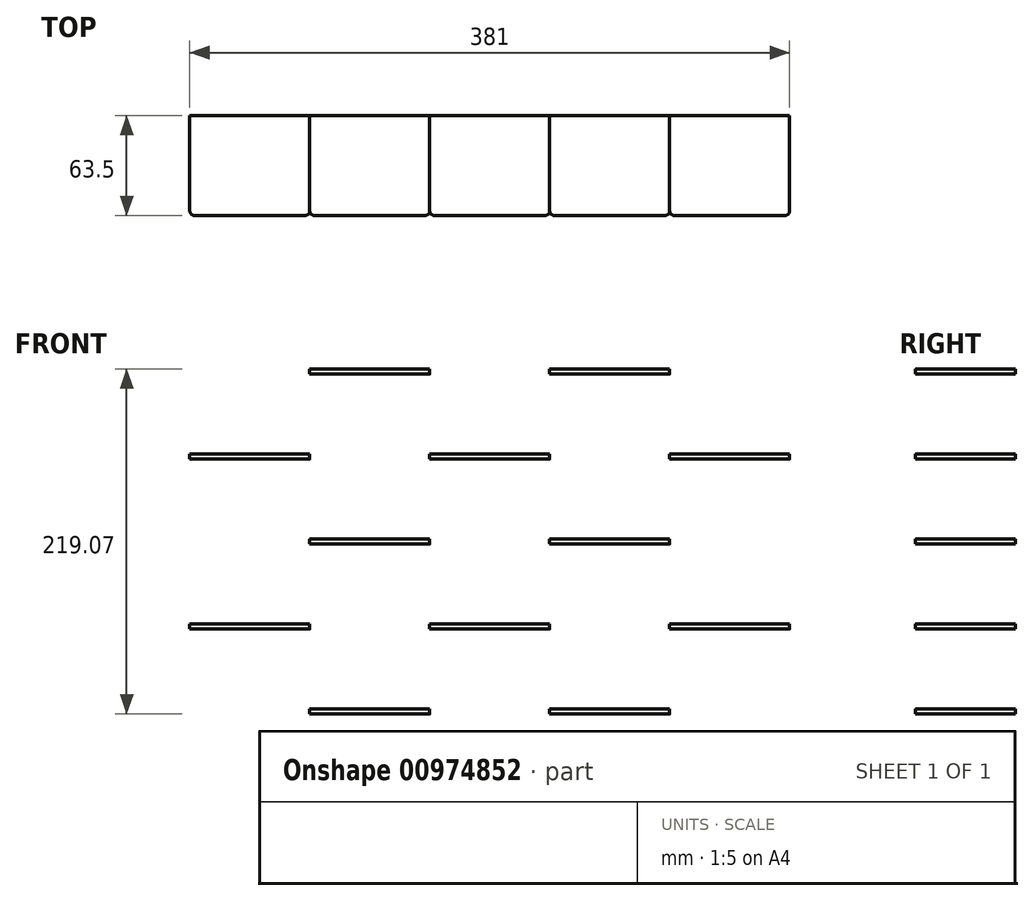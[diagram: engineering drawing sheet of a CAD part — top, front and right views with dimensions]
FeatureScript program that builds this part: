
annotation { "Feature Type Name" : "Feature", "Feature Type Description" : "" }
export const myFeature = defineFeature(function(context is Context, id is Id, definition is map)
    precondition{}
    {
        {
            var Q0;
            Q0=qCreatedBy(makeId("Front.planeOp"),FACE);
            var sketch = newSketch(context, id + "F0", { "sketchPlane" : qUnion([Q0])});
            skLineSegment(sketch, "E0.bottom", {"start": v(-97.67, 0) * mm, "end": v(-21.47, 0) * mm});
            skLineSegment(sketch, "E0.top", {"start": v(-97.67, -3.18) * mm, "end": v(-21.47, -3.18) * mm});
            skLineSegment(sketch, "E0.left", {"start": v(-97.67, 0) * mm, "end": v(-97.67, -3.18) * mm});
            skLineSegment(sketch, "E0.right", {"start": v(-21.47, 0) * mm, "end": v(-21.47, -3.18) * mm});
            skSolve(sketch);
        }
        {
            var Q0;
            Q0 = qSketchRegion(id + "F0", true);
            extrude(context, id + "F1", {"entities" : qUnion([Q0]), "depth" : 63.5 * mm, "offsetDistance" : 25.4 * mm});
        }
        {
            var Q0;
            Q0=makeQuery(id+"F1.opExtrude","CAP_EDGE",EDGE,{"disambiguationData":[OSD([sQuery(id+"F0.wireOp",EDGE,"E0.right")])],"isStart":false});
            fillet(context, id + "F2", {"entities" : qUnion([Q0]), "radius" : 3.17 * mm, "tangentPropagation" : true, "allowEdgeOverflow" : false});
        }
        {
            var Q0;
            Q0=makeQuery(id+"F1.opExtrude","CAP_EDGE",EDGE,{"disambiguationData":[OSD([sQuery(id+"F0.wireOp",EDGE,"E0.left")])],"isStart":false});
            fillet(context, id + "F3", {"entities" : qUnion([Q0]), "radius" : 3.17 * mm, "tangentPropagation" : true, "allowEdgeOverflow" : false});
        }
        {
            var Q0;
            Q0=makeQuery(id+"F1.opExtrude","SWEPT_BODY",BODY,{"disambiguationData":[OSD([sQuery(id+"F0.wireOp",EDGE,"E0.bottom"),sQuery(id+"F0.wireOp",EDGE,"E0.top"),sQuery(id+"F0.wireOp",EDGE,"E0.left"),sQuery(id+"F0.wireOp",EDGE,"E0.right")])]});
            transform(context, id + "F4", {"entities" : qUnion([Q0]), "transformType" : TransformType.TRANSLATION_3D, "dx" : 76.2 * mm, "dy" : 0 * mm, "dz" : 0 * mm, "makeCopy" : true});
        }
        {
            var Q0;
            Q0=makeQuery(id+"F4.opPattern","COPY",BODY,{"derivedFrom":makeQuery(id+"F1.opExtrude","SWEPT_BODY",BODY,{"disambiguationData":[OSD([sQuery(id+"F0.wireOp",EDGE,"E0.bottom"),sQuery(id+"F0.wireOp",EDGE,"E0.top"),sQuery(id+"F0.wireOp",EDGE,"E0.left"),sQuery(id+"F0.wireOp",EDGE,"E0.right")])]}),"instanceName":"1"});
            transform(context, id + "F5", {"entities" : qUnion([Q0]), "transformType" : TransformType.TRANSLATION_3D, "dx" : 76.2 * mm, "dy" : 0 * mm, "dz" : 0 * mm, "makeCopy" : true});
        }
        {
            var Q0;
            Q0=makeQuery(id+"F5.opPattern","COPY",BODY,{"derivedFrom":makeQuery(id+"F4.opPattern","COPY",BODY,{"derivedFrom":makeQuery(id+"F1.opExtrude","SWEPT_BODY",BODY,{"disambiguationData":[OSD([sQuery(id+"F0.wireOp",EDGE,"E0.bottom"),sQuery(id+"F0.wireOp",EDGE,"E0.top"),sQuery(id+"F0.wireOp",EDGE,"E0.left"),sQuery(id+"F0.wireOp",EDGE,"E0.right")])]}),"instanceName":"1"}),"instanceName":"1"});
            transform(context, id + "F6", {"entities" : qUnion([Q0]), "transformType" : TransformType.TRANSLATION_3D, "dx" : 76.2 * mm, "dy" : 0 * mm, "dz" : 0 * mm, "makeCopy" : true});
        }
        {
            var Q0;
            Q0=makeQuery(id+"F6.opPattern","COPY",BODY,{"derivedFrom":makeQuery(id+"F5.opPattern","COPY",BODY,{"derivedFrom":makeQuery(id+"F4.opPattern","COPY",BODY,{"derivedFrom":makeQuery(id+"F1.opExtrude","SWEPT_BODY",BODY,{"disambiguationData":[OSD([sQuery(id+"F0.wireOp",EDGE,"E0.bottom"),sQuery(id+"F0.wireOp",EDGE,"E0.top"),sQuery(id+"F0.wireOp",EDGE,"E0.left"),sQuery(id+"F0.wireOp",EDGE,"E0.right")])]}),"instanceName":"1"}),"instanceName":"1"}),"instanceName":"1"});
            transform(context, id + "F7", {"entities" : qUnion([Q0]), "transformType" : TransformType.TRANSLATION_3D, "dx" : 76.2 * mm, "dy" : 0 * mm, "dz" : 0 * mm, "makeCopy" : true});
        }
        {
            var Q0;
            Q0=makeQuery(id+"F1.opExtrude","SWEPT_BODY",BODY,{"disambiguationData":[OSD([sQuery(id+"F0.wireOp",EDGE,"E0.bottom"),sQuery(id+"F0.wireOp",EDGE,"E0.top"),sQuery(id+"F0.wireOp",EDGE,"E0.left"),sQuery(id+"F0.wireOp",EDGE,"E0.right")])]});
            var Q1;
            Q1=makeQuery(id+"F4.opPattern","COPY",BODY,{"derivedFrom":makeQuery(id+"F1.opExtrude","SWEPT_BODY",BODY,{"disambiguationData":[OSD([sQuery(id+"F0.wireOp",EDGE,"E0.bottom"),sQuery(id+"F0.wireOp",EDGE,"E0.top"),sQuery(id+"F0.wireOp",EDGE,"E0.left"),sQuery(id+"F0.wireOp",EDGE,"E0.right")])]}),"instanceName":"1"});
            var Q2;
            Q2=makeQuery(id+"F5.opPattern","COPY",BODY,{"derivedFrom":makeQuery(id+"F4.opPattern","COPY",BODY,{"derivedFrom":makeQuery(id+"F1.opExtrude","SWEPT_BODY",BODY,{"disambiguationData":[OSD([sQuery(id+"F0.wireOp",EDGE,"E0.bottom"),sQuery(id+"F0.wireOp",EDGE,"E0.top"),sQuery(id+"F0.wireOp",EDGE,"E0.left"),sQuery(id+"F0.wireOp",EDGE,"E0.right")])]}),"instanceName":"1"}),"instanceName":"1"});
            var Q3;
            Q3=makeQuery(id+"F6.opPattern","COPY",BODY,{"derivedFrom":makeQuery(id+"F5.opPattern","COPY",BODY,{"derivedFrom":makeQuery(id+"F4.opPattern","COPY",BODY,{"derivedFrom":makeQuery(id+"F1.opExtrude","SWEPT_BODY",BODY,{"disambiguationData":[OSD([sQuery(id+"F0.wireOp",EDGE,"E0.bottom"),sQuery(id+"F0.wireOp",EDGE,"E0.top"),sQuery(id+"F0.wireOp",EDGE,"E0.left"),sQuery(id+"F0.wireOp",EDGE,"E0.right")])]}),"instanceName":"1"}),"instanceName":"1"}),"instanceName":"1"});
            var Q4;
            Q4=makeQuery(id+"F7.opPattern","COPY",BODY,{"derivedFrom":makeQuery(id+"F6.opPattern","COPY",BODY,{"derivedFrom":makeQuery(id+"F5.opPattern","COPY",BODY,{"derivedFrom":makeQuery(id+"F4.opPattern","COPY",BODY,{"derivedFrom":makeQuery(id+"F1.opExtrude","SWEPT_BODY",BODY,{"disambiguationData":[OSD([sQuery(id+"F0.wireOp",EDGE,"E0.bottom"),sQuery(id+"F0.wireOp",EDGE,"E0.top"),sQuery(id+"F0.wireOp",EDGE,"E0.left"),sQuery(id+"F0.wireOp",EDGE,"E0.right")])]}),"instanceName":"1"}),"instanceName":"1"}),"instanceName":"1"}),"instanceName":"1"});
            transform(context, id + "F8", {"entities" : qUnion([Q0, Q1, Q2, Q3, Q4]), "transformType" : TransformType.TRANSLATION_3D, "dx" : 0 * mm, "dy" : 0 * mm, "dz" : 104.77 * mm, "makeCopy" : true});
        }
        {
            var Q0;
            Q0=makeQuery(id+"F8.opPattern","COPY",BODY,{"derivedFrom":makeQuery(id+"F1.opExtrude","SWEPT_BODY",BODY,{"disambiguationData":[OSD([sQuery(id+"F0.wireOp",EDGE,"E0.bottom"),sQuery(id+"F0.wireOp",EDGE,"E0.top"),sQuery(id+"F0.wireOp",EDGE,"E0.left"),sQuery(id+"F0.wireOp",EDGE,"E0.right")])]}),"instanceName":"1"});
            var Q1;
            Q1=makeQuery(id+"F8.opPattern","COPY",BODY,{"derivedFrom":makeQuery(id+"F4.opPattern","COPY",BODY,{"derivedFrom":makeQuery(id+"F1.opExtrude","SWEPT_BODY",BODY,{"disambiguationData":[OSD([sQuery(id+"F0.wireOp",EDGE,"E0.bottom"),sQuery(id+"F0.wireOp",EDGE,"E0.top"),sQuery(id+"F0.wireOp",EDGE,"E0.left"),sQuery(id+"F0.wireOp",EDGE,"E0.right")])]}),"instanceName":"1"}),"instanceName":"1"});
            var Q2;
            Q2=makeQuery(id+"F8.opPattern","COPY",BODY,{"derivedFrom":makeQuery(id+"F6.opPattern","COPY",BODY,{"derivedFrom":makeQuery(id+"F5.opPattern","COPY",BODY,{"derivedFrom":makeQuery(id+"F4.opPattern","COPY",BODY,{"derivedFrom":makeQuery(id+"F1.opExtrude","SWEPT_BODY",BODY,{"disambiguationData":[OSD([sQuery(id+"F0.wireOp",EDGE,"E0.bottom"),sQuery(id+"F0.wireOp",EDGE,"E0.top"),sQuery(id+"F0.wireOp",EDGE,"E0.left"),sQuery(id+"F0.wireOp",EDGE,"E0.right")])]}),"instanceName":"1"}),"instanceName":"1"}),"instanceName":"1"}),"instanceName":"1"});
            var Q3;
            Q3=makeQuery(id+"F8.opPattern","COPY",BODY,{"derivedFrom":makeQuery(id+"F7.opPattern","COPY",BODY,{"derivedFrom":makeQuery(id+"F6.opPattern","COPY",BODY,{"derivedFrom":makeQuery(id+"F5.opPattern","COPY",BODY,{"derivedFrom":makeQuery(id+"F4.opPattern","COPY",BODY,{"derivedFrom":makeQuery(id+"F1.opExtrude","SWEPT_BODY",BODY,{"disambiguationData":[OSD([sQuery(id+"F0.wireOp",EDGE,"E0.bottom"),sQuery(id+"F0.wireOp",EDGE,"E0.top"),sQuery(id+"F0.wireOp",EDGE,"E0.left"),sQuery(id+"F0.wireOp",EDGE,"E0.right")])]}),"instanceName":"1"}),"instanceName":"1"}),"instanceName":"1"}),"instanceName":"1"}),"instanceName":"1"});
            var Q4;
            Q4=makeQuery(id+"F8.opPattern","COPY",BODY,{"derivedFrom":makeQuery(id+"F5.opPattern","COPY",BODY,{"derivedFrom":makeQuery(id+"F4.opPattern","COPY",BODY,{"derivedFrom":makeQuery(id+"F1.opExtrude","SWEPT_BODY",BODY,{"disambiguationData":[OSD([sQuery(id+"F0.wireOp",EDGE,"E0.bottom"),sQuery(id+"F0.wireOp",EDGE,"E0.top"),sQuery(id+"F0.wireOp",EDGE,"E0.left"),sQuery(id+"F0.wireOp",EDGE,"E0.right")])]}),"instanceName":"1"}),"instanceName":"1"}),"instanceName":"1"});
            transform(context, id + "F9", {"entities" : qUnion([Q0, Q1, Q2, Q3, Q4]), "transformType" : TransformType.TRANSLATION_3D, "dx" : 0 * mm, "dy" : 0 * mm, "dz" : 127 * mm, "makeCopy" : true});
        }
        {
            var Q0;
            Q0=makeQuery(id+"F9.opPattern","COPY",BODY,{"derivedFrom":makeQuery(id+"F8.opPattern","COPY",BODY,{"derivedFrom":makeQuery(id+"F1.opExtrude","SWEPT_BODY",BODY,{"disambiguationData":[OSD([sQuery(id+"F0.wireOp",EDGE,"E0.bottom"),sQuery(id+"F0.wireOp",EDGE,"E0.top"),sQuery(id+"F0.wireOp",EDGE,"E0.left"),sQuery(id+"F0.wireOp",EDGE,"E0.right")])]}),"instanceName":"1"}),"instanceName":"1"});
            var Q1;
            Q1=makeQuery(id+"F9.opPattern","COPY",BODY,{"derivedFrom":makeQuery(id+"F8.opPattern","COPY",BODY,{"derivedFrom":makeQuery(id+"F4.opPattern","COPY",BODY,{"derivedFrom":makeQuery(id+"F1.opExtrude","SWEPT_BODY",BODY,{"disambiguationData":[OSD([sQuery(id+"F0.wireOp",EDGE,"E0.bottom"),sQuery(id+"F0.wireOp",EDGE,"E0.top"),sQuery(id+"F0.wireOp",EDGE,"E0.left"),sQuery(id+"F0.wireOp",EDGE,"E0.right")])]}),"instanceName":"1"}),"instanceName":"1"}),"instanceName":"1"});
            var Q2;
            Q2=makeQuery(id+"F9.opPattern","COPY",BODY,{"derivedFrom":makeQuery(id+"F8.opPattern","COPY",BODY,{"derivedFrom":makeQuery(id+"F5.opPattern","COPY",BODY,{"derivedFrom":makeQuery(id+"F4.opPattern","COPY",BODY,{"derivedFrom":makeQuery(id+"F1.opExtrude","SWEPT_BODY",BODY,{"disambiguationData":[OSD([sQuery(id+"F0.wireOp",EDGE,"E0.bottom"),sQuery(id+"F0.wireOp",EDGE,"E0.top"),sQuery(id+"F0.wireOp",EDGE,"E0.left"),sQuery(id+"F0.wireOp",EDGE,"E0.right")])]}),"instanceName":"1"}),"instanceName":"1"}),"instanceName":"1"}),"instanceName":"1"});
            var Q3;
            Q3=makeQuery(id+"F9.opPattern","COPY",BODY,{"derivedFrom":makeQuery(id+"F8.opPattern","COPY",BODY,{"derivedFrom":makeQuery(id+"F6.opPattern","COPY",BODY,{"derivedFrom":makeQuery(id+"F5.opPattern","COPY",BODY,{"derivedFrom":makeQuery(id+"F4.opPattern","COPY",BODY,{"derivedFrom":makeQuery(id+"F1.opExtrude","SWEPT_BODY",BODY,{"disambiguationData":[OSD([sQuery(id+"F0.wireOp",EDGE,"E0.bottom"),sQuery(id+"F0.wireOp",EDGE,"E0.top"),sQuery(id+"F0.wireOp",EDGE,"E0.left"),sQuery(id+"F0.wireOp",EDGE,"E0.right")])]}),"instanceName":"1"}),"instanceName":"1"}),"instanceName":"1"}),"instanceName":"1"}),"instanceName":"1"});
            var Q4;
            Q4=makeQuery(id+"F9.opPattern","COPY",BODY,{"derivedFrom":makeQuery(id+"F8.opPattern","COPY",BODY,{"derivedFrom":makeQuery(id+"F7.opPattern","COPY",BODY,{"derivedFrom":makeQuery(id+"F6.opPattern","COPY",BODY,{"derivedFrom":makeQuery(id+"F5.opPattern","COPY",BODY,{"derivedFrom":makeQuery(id+"F4.opPattern","COPY",BODY,{"derivedFrom":makeQuery(id+"F1.opExtrude","SWEPT_BODY",BODY,{"disambiguationData":[OSD([sQuery(id+"F0.wireOp",EDGE,"E0.bottom"),sQuery(id+"F0.wireOp",EDGE,"E0.top"),sQuery(id+"F0.wireOp",EDGE,"E0.left"),sQuery(id+"F0.wireOp",EDGE,"E0.right")])]}),"instanceName":"1"}),"instanceName":"1"}),"instanceName":"1"}),"instanceName":"1"}),"instanceName":"1"}),"instanceName":"1"});
            transform(context, id + "F10", {"entities" : qUnion([Q0, Q1, Q2, Q3, Q4]), "transformType" : TransformType.TRANSLATION_3D, "dx" : 0 * mm, "dy" : 0 * mm, "dz" : 104.77 * mm, "makeCopy" : true});
        }
        {
            var Q0;
            Q0=makeQuery(id+"F10.opPattern","COPY",BODY,{"derivedFrom":makeQuery(id+"F9.opPattern","COPY",BODY,{"derivedFrom":makeQuery(id+"F8.opPattern","COPY",BODY,{"derivedFrom":makeQuery(id+"F1.opExtrude","SWEPT_BODY",BODY,{"disambiguationData":[OSD([sQuery(id+"F0.wireOp",EDGE,"E0.bottom"),sQuery(id+"F0.wireOp",EDGE,"E0.top"),sQuery(id+"F0.wireOp",EDGE,"E0.left"),sQuery(id+"F0.wireOp",EDGE,"E0.right")])]}),"instanceName":"1"}),"instanceName":"1"}),"instanceName":"1"});
            var Q1;
            Q1=makeQuery(id+"F10.opPattern","COPY",BODY,{"derivedFrom":makeQuery(id+"F9.opPattern","COPY",BODY,{"derivedFrom":makeQuery(id+"F8.opPattern","COPY",BODY,{"derivedFrom":makeQuery(id+"F4.opPattern","COPY",BODY,{"derivedFrom":makeQuery(id+"F1.opExtrude","SWEPT_BODY",BODY,{"disambiguationData":[OSD([sQuery(id+"F0.wireOp",EDGE,"E0.bottom"),sQuery(id+"F0.wireOp",EDGE,"E0.top"),sQuery(id+"F0.wireOp",EDGE,"E0.left"),sQuery(id+"F0.wireOp",EDGE,"E0.right")])]}),"instanceName":"1"}),"instanceName":"1"}),"instanceName":"1"}),"instanceName":"1"});
            var Q2;
            Q2=makeQuery(id+"F10.opPattern","COPY",BODY,{"derivedFrom":makeQuery(id+"F9.opPattern","COPY",BODY,{"derivedFrom":makeQuery(id+"F8.opPattern","COPY",BODY,{"derivedFrom":makeQuery(id+"F5.opPattern","COPY",BODY,{"derivedFrom":makeQuery(id+"F4.opPattern","COPY",BODY,{"derivedFrom":makeQuery(id+"F1.opExtrude","SWEPT_BODY",BODY,{"disambiguationData":[OSD([sQuery(id+"F0.wireOp",EDGE,"E0.bottom"),sQuery(id+"F0.wireOp",EDGE,"E0.top"),sQuery(id+"F0.wireOp",EDGE,"E0.left"),sQuery(id+"F0.wireOp",EDGE,"E0.right")])]}),"instanceName":"1"}),"instanceName":"1"}),"instanceName":"1"}),"instanceName":"1"}),"instanceName":"1"});
            var Q3;
            Q3=makeQuery(id+"F10.opPattern","COPY",BODY,{"derivedFrom":makeQuery(id+"F9.opPattern","COPY",BODY,{"derivedFrom":makeQuery(id+"F8.opPattern","COPY",BODY,{"derivedFrom":makeQuery(id+"F6.opPattern","COPY",BODY,{"derivedFrom":makeQuery(id+"F5.opPattern","COPY",BODY,{"derivedFrom":makeQuery(id+"F4.opPattern","COPY",BODY,{"derivedFrom":makeQuery(id+"F1.opExtrude","SWEPT_BODY",BODY,{"disambiguationData":[OSD([sQuery(id+"F0.wireOp",EDGE,"E0.bottom"),sQuery(id+"F0.wireOp",EDGE,"E0.top"),sQuery(id+"F0.wireOp",EDGE,"E0.left"),sQuery(id+"F0.wireOp",EDGE,"E0.right")])]}),"instanceName":"1"}),"instanceName":"1"}),"instanceName":"1"}),"instanceName":"1"}),"instanceName":"1"}),"instanceName":"1"});
            var Q4;
            Q4=makeQuery(id+"F10.opPattern","COPY",BODY,{"derivedFrom":makeQuery(id+"F9.opPattern","COPY",BODY,{"derivedFrom":makeQuery(id+"F8.opPattern","COPY",BODY,{"derivedFrom":makeQuery(id+"F7.opPattern","COPY",BODY,{"derivedFrom":makeQuery(id+"F6.opPattern","COPY",BODY,{"derivedFrom":makeQuery(id+"F5.opPattern","COPY",BODY,{"derivedFrom":makeQuery(id+"F4.opPattern","COPY",BODY,{"derivedFrom":makeQuery(id+"F1.opExtrude","SWEPT_BODY",BODY,{"disambiguationData":[OSD([sQuery(id+"F0.wireOp",EDGE,"E0.bottom"),sQuery(id+"F0.wireOp",EDGE,"E0.top"),sQuery(id+"F0.wireOp",EDGE,"E0.left"),sQuery(id+"F0.wireOp",EDGE,"E0.right")])]}),"instanceName":"1"}),"instanceName":"1"}),"instanceName":"1"}),"instanceName":"1"}),"instanceName":"1"}),"instanceName":"1"}),"instanceName":"1"});
            transform(context, id + "F11", {"entities" : qUnion([Q0, Q1, Q2, Q3, Q4]), "transformType" : TransformType.TRANSLATION_3D, "dx" : 0 * mm, "dy" : 0 * mm, "dz" : 104.77 * mm, "makeCopy" : true});
        }
        {
            var Q0;
            Q0=makeQuery(id+"F10.opPattern","COPY",BODY,{"derivedFrom":makeQuery(id+"F9.opPattern","COPY",BODY,{"derivedFrom":makeQuery(id+"F8.opPattern","COPY",BODY,{"derivedFrom":makeQuery(id+"F7.opPattern","COPY",BODY,{"derivedFrom":makeQuery(id+"F6.opPattern","COPY",BODY,{"derivedFrom":makeQuery(id+"F5.opPattern","COPY",BODY,{"derivedFrom":makeQuery(id+"F4.opPattern","COPY",BODY,{"derivedFrom":makeQuery(id+"F1.opExtrude","SWEPT_BODY",BODY,{"disambiguationData":[OSD([sQuery(id+"F0.wireOp",EDGE,"E0.bottom"),sQuery(id+"F0.wireOp",EDGE,"E0.top"),sQuery(id+"F0.wireOp",EDGE,"E0.left"),sQuery(id+"F0.wireOp",EDGE,"E0.right")])]}),"instanceName":"1"}),"instanceName":"1"}),"instanceName":"1"}),"instanceName":"1"}),"instanceName":"1"}),"instanceName":"1"}),"instanceName":"1"});
            var Q1;
            Q1=makeQuery(id+"F10.opPattern","COPY",BODY,{"derivedFrom":makeQuery(id+"F9.opPattern","COPY",BODY,{"derivedFrom":makeQuery(id+"F8.opPattern","COPY",BODY,{"derivedFrom":makeQuery(id+"F6.opPattern","COPY",BODY,{"derivedFrom":makeQuery(id+"F5.opPattern","COPY",BODY,{"derivedFrom":makeQuery(id+"F4.opPattern","COPY",BODY,{"derivedFrom":makeQuery(id+"F1.opExtrude","SWEPT_BODY",BODY,{"disambiguationData":[OSD([sQuery(id+"F0.wireOp",EDGE,"E0.bottom"),sQuery(id+"F0.wireOp",EDGE,"E0.top"),sQuery(id+"F0.wireOp",EDGE,"E0.left"),sQuery(id+"F0.wireOp",EDGE,"E0.right")])]}),"instanceName":"1"}),"instanceName":"1"}),"instanceName":"1"}),"instanceName":"1"}),"instanceName":"1"}),"instanceName":"1"});
            var Q2;
            Q2=makeQuery(id+"F10.opPattern","COPY",BODY,{"derivedFrom":makeQuery(id+"F9.opPattern","COPY",BODY,{"derivedFrom":makeQuery(id+"F8.opPattern","COPY",BODY,{"derivedFrom":makeQuery(id+"F5.opPattern","COPY",BODY,{"derivedFrom":makeQuery(id+"F4.opPattern","COPY",BODY,{"derivedFrom":makeQuery(id+"F1.opExtrude","SWEPT_BODY",BODY,{"disambiguationData":[OSD([sQuery(id+"F0.wireOp",EDGE,"E0.bottom"),sQuery(id+"F0.wireOp",EDGE,"E0.top"),sQuery(id+"F0.wireOp",EDGE,"E0.left"),sQuery(id+"F0.wireOp",EDGE,"E0.right")])]}),"instanceName":"1"}),"instanceName":"1"}),"instanceName":"1"}),"instanceName":"1"}),"instanceName":"1"});
            var Q3;
            Q3=makeQuery(id+"F10.opPattern","COPY",BODY,{"derivedFrom":makeQuery(id+"F9.opPattern","COPY",BODY,{"derivedFrom":makeQuery(id+"F8.opPattern","COPY",BODY,{"derivedFrom":makeQuery(id+"F4.opPattern","COPY",BODY,{"derivedFrom":makeQuery(id+"F1.opExtrude","SWEPT_BODY",BODY,{"disambiguationData":[OSD([sQuery(id+"F0.wireOp",EDGE,"E0.bottom"),sQuery(id+"F0.wireOp",EDGE,"E0.top"),sQuery(id+"F0.wireOp",EDGE,"E0.left"),sQuery(id+"F0.wireOp",EDGE,"E0.right")])]}),"instanceName":"1"}),"instanceName":"1"}),"instanceName":"1"}),"instanceName":"1"});
            var Q4;
            Q4=makeQuery(id+"F10.opPattern","COPY",BODY,{"derivedFrom":makeQuery(id+"F9.opPattern","COPY",BODY,{"derivedFrom":makeQuery(id+"F8.opPattern","COPY",BODY,{"derivedFrom":makeQuery(id+"F1.opExtrude","SWEPT_BODY",BODY,{"disambiguationData":[OSD([sQuery(id+"F0.wireOp",EDGE,"E0.bottom"),sQuery(id+"F0.wireOp",EDGE,"E0.top"),sQuery(id+"F0.wireOp",EDGE,"E0.left"),sQuery(id+"F0.wireOp",EDGE,"E0.right")])]}),"instanceName":"1"}),"instanceName":"1"}),"instanceName":"1"});
            var Q5;
            Q5=makeQuery(id+"F9.opPattern","COPY",BODY,{"derivedFrom":makeQuery(id+"F8.opPattern","COPY",BODY,{"derivedFrom":makeQuery(id+"F1.opExtrude","SWEPT_BODY",BODY,{"disambiguationData":[OSD([sQuery(id+"F0.wireOp",EDGE,"E0.bottom"),sQuery(id+"F0.wireOp",EDGE,"E0.top"),sQuery(id+"F0.wireOp",EDGE,"E0.left"),sQuery(id+"F0.wireOp",EDGE,"E0.right")])]}),"instanceName":"1"}),"instanceName":"1"});
            var Q6;
            Q6=makeQuery(id+"F9.opPattern","COPY",BODY,{"derivedFrom":makeQuery(id+"F8.opPattern","COPY",BODY,{"derivedFrom":makeQuery(id+"F4.opPattern","COPY",BODY,{"derivedFrom":makeQuery(id+"F1.opExtrude","SWEPT_BODY",BODY,{"disambiguationData":[OSD([sQuery(id+"F0.wireOp",EDGE,"E0.bottom"),sQuery(id+"F0.wireOp",EDGE,"E0.top"),sQuery(id+"F0.wireOp",EDGE,"E0.left"),sQuery(id+"F0.wireOp",EDGE,"E0.right")])]}),"instanceName":"1"}),"instanceName":"1"}),"instanceName":"1"});
            var Q7;
            Q7=makeQuery(id+"F9.opPattern","COPY",BODY,{"derivedFrom":makeQuery(id+"F8.opPattern","COPY",BODY,{"derivedFrom":makeQuery(id+"F6.opPattern","COPY",BODY,{"derivedFrom":makeQuery(id+"F5.opPattern","COPY",BODY,{"derivedFrom":makeQuery(id+"F4.opPattern","COPY",BODY,{"derivedFrom":makeQuery(id+"F1.opExtrude","SWEPT_BODY",BODY,{"disambiguationData":[OSD([sQuery(id+"F0.wireOp",EDGE,"E0.bottom"),sQuery(id+"F0.wireOp",EDGE,"E0.top"),sQuery(id+"F0.wireOp",EDGE,"E0.left"),sQuery(id+"F0.wireOp",EDGE,"E0.right")])]}),"instanceName":"1"}),"instanceName":"1"}),"instanceName":"1"}),"instanceName":"1"}),"instanceName":"1"});
            var Q8;
            Q8=makeQuery(id+"F9.opPattern","COPY",BODY,{"derivedFrom":makeQuery(id+"F8.opPattern","COPY",BODY,{"derivedFrom":makeQuery(id+"F7.opPattern","COPY",BODY,{"derivedFrom":makeQuery(id+"F6.opPattern","COPY",BODY,{"derivedFrom":makeQuery(id+"F5.opPattern","COPY",BODY,{"derivedFrom":makeQuery(id+"F4.opPattern","COPY",BODY,{"derivedFrom":makeQuery(id+"F1.opExtrude","SWEPT_BODY",BODY,{"disambiguationData":[OSD([sQuery(id+"F0.wireOp",EDGE,"E0.bottom"),sQuery(id+"F0.wireOp",EDGE,"E0.top"),sQuery(id+"F0.wireOp",EDGE,"E0.left"),sQuery(id+"F0.wireOp",EDGE,"E0.right")])]}),"instanceName":"1"}),"instanceName":"1"}),"instanceName":"1"}),"instanceName":"1"}),"instanceName":"1"}),"instanceName":"1"});
            var Q9;
            Q9=makeQuery(id+"F9.opPattern","COPY",BODY,{"derivedFrom":makeQuery(id+"F8.opPattern","COPY",BODY,{"derivedFrom":makeQuery(id+"F5.opPattern","COPY",BODY,{"derivedFrom":makeQuery(id+"F4.opPattern","COPY",BODY,{"derivedFrom":makeQuery(id+"F1.opExtrude","SWEPT_BODY",BODY,{"disambiguationData":[OSD([sQuery(id+"F0.wireOp",EDGE,"E0.bottom"),sQuery(id+"F0.wireOp",EDGE,"E0.top"),sQuery(id+"F0.wireOp",EDGE,"E0.left"),sQuery(id+"F0.wireOp",EDGE,"E0.right")])]}),"instanceName":"1"}),"instanceName":"1"}),"instanceName":"1"}),"instanceName":"1"});
            transform(context, id + "F12", {"entities" : qUnion([Q0, Q1, Q2, Q3, Q4, Q5, Q6, Q7, Q8, Q9]), "transformType" : TransformType.TRANSLATION_3D, "dx" : 0 * mm, "dy" : 0 * mm, "dz" : -3.17 * mm, "makeCopy" : false});
        }
        {
            var Q0;
            Q0=makeQuery(id+"F8.opPattern","COPY",BODY,{"derivedFrom":makeQuery(id+"F1.opExtrude","SWEPT_BODY",BODY,{"disambiguationData":[OSD([sQuery(id+"F0.wireOp",EDGE,"E0.bottom"),sQuery(id+"F0.wireOp",EDGE,"E0.top"),sQuery(id+"F0.wireOp",EDGE,"E0.left"),sQuery(id+"F0.wireOp",EDGE,"E0.right")])]}),"instanceName":"1"});
            var Q1;
            Q1=makeQuery(id+"F11.opPattern","COPY",BODY,{"derivedFrom":makeQuery(id+"F10.opPattern","COPY",BODY,{"derivedFrom":makeQuery(id+"F9.opPattern","COPY",BODY,{"derivedFrom":makeQuery(id+"F8.opPattern","COPY",BODY,{"derivedFrom":makeQuery(id+"F7.opPattern","COPY",BODY,{"derivedFrom":makeQuery(id+"F6.opPattern","COPY",BODY,{"derivedFrom":makeQuery(id+"F5.opPattern","COPY",BODY,{"derivedFrom":makeQuery(id+"F4.opPattern","COPY",BODY,{"derivedFrom":makeQuery(id+"F1.opExtrude","SWEPT_BODY",BODY,{"disambiguationData":[OSD([sQuery(id+"F0.wireOp",EDGE,"E0.bottom"),sQuery(id+"F0.wireOp",EDGE,"E0.top"),sQuery(id+"F0.wireOp",EDGE,"E0.left"),sQuery(id+"F0.wireOp",EDGE,"E0.right")])]}),"instanceName":"1"}),"instanceName":"1"}),"instanceName":"1"}),"instanceName":"1"}),"instanceName":"1"}),"instanceName":"1"}),"instanceName":"1"}),"instanceName":"1"});
            var Q2;
            Q2=makeQuery(id+"F8.opPattern","COPY",BODY,{"derivedFrom":makeQuery(id+"F4.opPattern","COPY",BODY,{"derivedFrom":makeQuery(id+"F1.opExtrude","SWEPT_BODY",BODY,{"disambiguationData":[OSD([sQuery(id+"F0.wireOp",EDGE,"E0.bottom"),sQuery(id+"F0.wireOp",EDGE,"E0.top"),sQuery(id+"F0.wireOp",EDGE,"E0.left"),sQuery(id+"F0.wireOp",EDGE,"E0.right")])]}),"instanceName":"1"}),"instanceName":"1"});
            var Q3;
            Q3=makeQuery(id+"F8.opPattern","COPY",BODY,{"derivedFrom":makeQuery(id+"F5.opPattern","COPY",BODY,{"derivedFrom":makeQuery(id+"F4.opPattern","COPY",BODY,{"derivedFrom":makeQuery(id+"F1.opExtrude","SWEPT_BODY",BODY,{"disambiguationData":[OSD([sQuery(id+"F0.wireOp",EDGE,"E0.bottom"),sQuery(id+"F0.wireOp",EDGE,"E0.top"),sQuery(id+"F0.wireOp",EDGE,"E0.left"),sQuery(id+"F0.wireOp",EDGE,"E0.right")])]}),"instanceName":"1"}),"instanceName":"1"}),"instanceName":"1"});
            var Q4;
            Q4=makeQuery(id+"F8.opPattern","COPY",BODY,{"derivedFrom":makeQuery(id+"F6.opPattern","COPY",BODY,{"derivedFrom":makeQuery(id+"F5.opPattern","COPY",BODY,{"derivedFrom":makeQuery(id+"F4.opPattern","COPY",BODY,{"derivedFrom":makeQuery(id+"F1.opExtrude","SWEPT_BODY",BODY,{"disambiguationData":[OSD([sQuery(id+"F0.wireOp",EDGE,"E0.bottom"),sQuery(id+"F0.wireOp",EDGE,"E0.top"),sQuery(id+"F0.wireOp",EDGE,"E0.left"),sQuery(id+"F0.wireOp",EDGE,"E0.right")])]}),"instanceName":"1"}),"instanceName":"1"}),"instanceName":"1"}),"instanceName":"1"});
            var Q5;
            Q5=makeQuery(id+"F8.opPattern","COPY",BODY,{"derivedFrom":makeQuery(id+"F7.opPattern","COPY",BODY,{"derivedFrom":makeQuery(id+"F6.opPattern","COPY",BODY,{"derivedFrom":makeQuery(id+"F5.opPattern","COPY",BODY,{"derivedFrom":makeQuery(id+"F4.opPattern","COPY",BODY,{"derivedFrom":makeQuery(id+"F1.opExtrude","SWEPT_BODY",BODY,{"disambiguationData":[OSD([sQuery(id+"F0.wireOp",EDGE,"E0.bottom"),sQuery(id+"F0.wireOp",EDGE,"E0.top"),sQuery(id+"F0.wireOp",EDGE,"E0.left"),sQuery(id+"F0.wireOp",EDGE,"E0.right")])]}),"instanceName":"1"}),"instanceName":"1"}),"instanceName":"1"}),"instanceName":"1"}),"instanceName":"1"});
            var Q6;
            Q6=makeQuery(id+"F9.opPattern","COPY",BODY,{"derivedFrom":makeQuery(id+"F8.opPattern","COPY",BODY,{"derivedFrom":makeQuery(id+"F1.opExtrude","SWEPT_BODY",BODY,{"disambiguationData":[OSD([sQuery(id+"F0.wireOp",EDGE,"E0.bottom"),sQuery(id+"F0.wireOp",EDGE,"E0.top"),sQuery(id+"F0.wireOp",EDGE,"E0.left"),sQuery(id+"F0.wireOp",EDGE,"E0.right")])]}),"instanceName":"1"}),"instanceName":"1"});
            var Q7;
            Q7=makeQuery(id+"F9.opPattern","COPY",BODY,{"derivedFrom":makeQuery(id+"F8.opPattern","COPY",BODY,{"derivedFrom":makeQuery(id+"F4.opPattern","COPY",BODY,{"derivedFrom":makeQuery(id+"F1.opExtrude","SWEPT_BODY",BODY,{"disambiguationData":[OSD([sQuery(id+"F0.wireOp",EDGE,"E0.bottom"),sQuery(id+"F0.wireOp",EDGE,"E0.top"),sQuery(id+"F0.wireOp",EDGE,"E0.left"),sQuery(id+"F0.wireOp",EDGE,"E0.right")])]}),"instanceName":"1"}),"instanceName":"1"}),"instanceName":"1"});
            var Q8;
            Q8=makeQuery(id+"F9.opPattern","COPY",BODY,{"derivedFrom":makeQuery(id+"F8.opPattern","COPY",BODY,{"derivedFrom":makeQuery(id+"F5.opPattern","COPY",BODY,{"derivedFrom":makeQuery(id+"F4.opPattern","COPY",BODY,{"derivedFrom":makeQuery(id+"F1.opExtrude","SWEPT_BODY",BODY,{"disambiguationData":[OSD([sQuery(id+"F0.wireOp",EDGE,"E0.bottom"),sQuery(id+"F0.wireOp",EDGE,"E0.top"),sQuery(id+"F0.wireOp",EDGE,"E0.left"),sQuery(id+"F0.wireOp",EDGE,"E0.right")])]}),"instanceName":"1"}),"instanceName":"1"}),"instanceName":"1"}),"instanceName":"1"});
            var Q9;
            Q9=makeQuery(id+"F9.opPattern","COPY",BODY,{"derivedFrom":makeQuery(id+"F8.opPattern","COPY",BODY,{"derivedFrom":makeQuery(id+"F6.opPattern","COPY",BODY,{"derivedFrom":makeQuery(id+"F5.opPattern","COPY",BODY,{"derivedFrom":makeQuery(id+"F4.opPattern","COPY",BODY,{"derivedFrom":makeQuery(id+"F1.opExtrude","SWEPT_BODY",BODY,{"disambiguationData":[OSD([sQuery(id+"F0.wireOp",EDGE,"E0.bottom"),sQuery(id+"F0.wireOp",EDGE,"E0.top"),sQuery(id+"F0.wireOp",EDGE,"E0.left"),sQuery(id+"F0.wireOp",EDGE,"E0.right")])]}),"instanceName":"1"}),"instanceName":"1"}),"instanceName":"1"}),"instanceName":"1"}),"instanceName":"1"});
            var Q10;
            Q10=makeQuery(id+"F9.opPattern","COPY",BODY,{"derivedFrom":makeQuery(id+"F8.opPattern","COPY",BODY,{"derivedFrom":makeQuery(id+"F7.opPattern","COPY",BODY,{"derivedFrom":makeQuery(id+"F6.opPattern","COPY",BODY,{"derivedFrom":makeQuery(id+"F5.opPattern","COPY",BODY,{"derivedFrom":makeQuery(id+"F4.opPattern","COPY",BODY,{"derivedFrom":makeQuery(id+"F1.opExtrude","SWEPT_BODY",BODY,{"disambiguationData":[OSD([sQuery(id+"F0.wireOp",EDGE,"E0.bottom"),sQuery(id+"F0.wireOp",EDGE,"E0.top"),sQuery(id+"F0.wireOp",EDGE,"E0.left"),sQuery(id+"F0.wireOp",EDGE,"E0.right")])]}),"instanceName":"1"}),"instanceName":"1"}),"instanceName":"1"}),"instanceName":"1"}),"instanceName":"1"}),"instanceName":"1"});
            var Q11;
            Q11=makeQuery(id+"F10.opPattern","COPY",BODY,{"derivedFrom":makeQuery(id+"F9.opPattern","COPY",BODY,{"derivedFrom":makeQuery(id+"F8.opPattern","COPY",BODY,{"derivedFrom":makeQuery(id+"F1.opExtrude","SWEPT_BODY",BODY,{"disambiguationData":[OSD([sQuery(id+"F0.wireOp",EDGE,"E0.bottom"),sQuery(id+"F0.wireOp",EDGE,"E0.top"),sQuery(id+"F0.wireOp",EDGE,"E0.left"),sQuery(id+"F0.wireOp",EDGE,"E0.right")])]}),"instanceName":"1"}),"instanceName":"1"}),"instanceName":"1"});
            var Q12;
            Q12=makeQuery(id+"F10.opPattern","COPY",BODY,{"derivedFrom":makeQuery(id+"F9.opPattern","COPY",BODY,{"derivedFrom":makeQuery(id+"F8.opPattern","COPY",BODY,{"derivedFrom":makeQuery(id+"F4.opPattern","COPY",BODY,{"derivedFrom":makeQuery(id+"F1.opExtrude","SWEPT_BODY",BODY,{"disambiguationData":[OSD([sQuery(id+"F0.wireOp",EDGE,"E0.bottom"),sQuery(id+"F0.wireOp",EDGE,"E0.top"),sQuery(id+"F0.wireOp",EDGE,"E0.left"),sQuery(id+"F0.wireOp",EDGE,"E0.right")])]}),"instanceName":"1"}),"instanceName":"1"}),"instanceName":"1"}),"instanceName":"1"});
            var Q13;
            Q13=makeQuery(id+"F10.opPattern","COPY",BODY,{"derivedFrom":makeQuery(id+"F9.opPattern","COPY",BODY,{"derivedFrom":makeQuery(id+"F8.opPattern","COPY",BODY,{"derivedFrom":makeQuery(id+"F5.opPattern","COPY",BODY,{"derivedFrom":makeQuery(id+"F4.opPattern","COPY",BODY,{"derivedFrom":makeQuery(id+"F1.opExtrude","SWEPT_BODY",BODY,{"disambiguationData":[OSD([sQuery(id+"F0.wireOp",EDGE,"E0.bottom"),sQuery(id+"F0.wireOp",EDGE,"E0.top"),sQuery(id+"F0.wireOp",EDGE,"E0.left"),sQuery(id+"F0.wireOp",EDGE,"E0.right")])]}),"instanceName":"1"}),"instanceName":"1"}),"instanceName":"1"}),"instanceName":"1"}),"instanceName":"1"});
            var Q14;
            Q14=makeQuery(id+"F10.opPattern","COPY",BODY,{"derivedFrom":makeQuery(id+"F9.opPattern","COPY",BODY,{"derivedFrom":makeQuery(id+"F8.opPattern","COPY",BODY,{"derivedFrom":makeQuery(id+"F6.opPattern","COPY",BODY,{"derivedFrom":makeQuery(id+"F5.opPattern","COPY",BODY,{"derivedFrom":makeQuery(id+"F4.opPattern","COPY",BODY,{"derivedFrom":makeQuery(id+"F1.opExtrude","SWEPT_BODY",BODY,{"disambiguationData":[OSD([sQuery(id+"F0.wireOp",EDGE,"E0.bottom"),sQuery(id+"F0.wireOp",EDGE,"E0.top"),sQuery(id+"F0.wireOp",EDGE,"E0.left"),sQuery(id+"F0.wireOp",EDGE,"E0.right")])]}),"instanceName":"1"}),"instanceName":"1"}),"instanceName":"1"}),"instanceName":"1"}),"instanceName":"1"}),"instanceName":"1"});
            var Q15;
            Q15=makeQuery(id+"F10.opPattern","COPY",BODY,{"derivedFrom":makeQuery(id+"F9.opPattern","COPY",BODY,{"derivedFrom":makeQuery(id+"F8.opPattern","COPY",BODY,{"derivedFrom":makeQuery(id+"F7.opPattern","COPY",BODY,{"derivedFrom":makeQuery(id+"F6.opPattern","COPY",BODY,{"derivedFrom":makeQuery(id+"F5.opPattern","COPY",BODY,{"derivedFrom":makeQuery(id+"F4.opPattern","COPY",BODY,{"derivedFrom":makeQuery(id+"F1.opExtrude","SWEPT_BODY",BODY,{"disambiguationData":[OSD([sQuery(id+"F0.wireOp",EDGE,"E0.bottom"),sQuery(id+"F0.wireOp",EDGE,"E0.top"),sQuery(id+"F0.wireOp",EDGE,"E0.left"),sQuery(id+"F0.wireOp",EDGE,"E0.right")])]}),"instanceName":"1"}),"instanceName":"1"}),"instanceName":"1"}),"instanceName":"1"}),"instanceName":"1"}),"instanceName":"1"}),"instanceName":"1"});
            var Q16;
            Q16=makeQuery(id+"F11.opPattern","COPY",BODY,{"derivedFrom":makeQuery(id+"F10.opPattern","COPY",BODY,{"derivedFrom":makeQuery(id+"F9.opPattern","COPY",BODY,{"derivedFrom":makeQuery(id+"F8.opPattern","COPY",BODY,{"derivedFrom":makeQuery(id+"F1.opExtrude","SWEPT_BODY",BODY,{"disambiguationData":[OSD([sQuery(id+"F0.wireOp",EDGE,"E0.bottom"),sQuery(id+"F0.wireOp",EDGE,"E0.top"),sQuery(id+"F0.wireOp",EDGE,"E0.left"),sQuery(id+"F0.wireOp",EDGE,"E0.right")])]}),"instanceName":"1"}),"instanceName":"1"}),"instanceName":"1"}),"instanceName":"1"});
            var Q17;
            Q17=makeQuery(id+"F11.opPattern","COPY",BODY,{"derivedFrom":makeQuery(id+"F10.opPattern","COPY",BODY,{"derivedFrom":makeQuery(id+"F9.opPattern","COPY",BODY,{"derivedFrom":makeQuery(id+"F8.opPattern","COPY",BODY,{"derivedFrom":makeQuery(id+"F4.opPattern","COPY",BODY,{"derivedFrom":makeQuery(id+"F1.opExtrude","SWEPT_BODY",BODY,{"disambiguationData":[OSD([sQuery(id+"F0.wireOp",EDGE,"E0.bottom"),sQuery(id+"F0.wireOp",EDGE,"E0.top"),sQuery(id+"F0.wireOp",EDGE,"E0.left"),sQuery(id+"F0.wireOp",EDGE,"E0.right")])]}),"instanceName":"1"}),"instanceName":"1"}),"instanceName":"1"}),"instanceName":"1"}),"instanceName":"1"});
            var Q18;
            Q18=makeQuery(id+"F11.opPattern","COPY",BODY,{"derivedFrom":makeQuery(id+"F10.opPattern","COPY",BODY,{"derivedFrom":makeQuery(id+"F9.opPattern","COPY",BODY,{"derivedFrom":makeQuery(id+"F8.opPattern","COPY",BODY,{"derivedFrom":makeQuery(id+"F5.opPattern","COPY",BODY,{"derivedFrom":makeQuery(id+"F4.opPattern","COPY",BODY,{"derivedFrom":makeQuery(id+"F1.opExtrude","SWEPT_BODY",BODY,{"disambiguationData":[OSD([sQuery(id+"F0.wireOp",EDGE,"E0.bottom"),sQuery(id+"F0.wireOp",EDGE,"E0.top"),sQuery(id+"F0.wireOp",EDGE,"E0.left"),sQuery(id+"F0.wireOp",EDGE,"E0.right")])]}),"instanceName":"1"}),"instanceName":"1"}),"instanceName":"1"}),"instanceName":"1"}),"instanceName":"1"}),"instanceName":"1"});
            var Q19;
            Q19=makeQuery(id+"F11.opPattern","COPY",BODY,{"derivedFrom":makeQuery(id+"F10.opPattern","COPY",BODY,{"derivedFrom":makeQuery(id+"F9.opPattern","COPY",BODY,{"derivedFrom":makeQuery(id+"F8.opPattern","COPY",BODY,{"derivedFrom":makeQuery(id+"F6.opPattern","COPY",BODY,{"derivedFrom":makeQuery(id+"F5.opPattern","COPY",BODY,{"derivedFrom":makeQuery(id+"F4.opPattern","COPY",BODY,{"derivedFrom":makeQuery(id+"F1.opExtrude","SWEPT_BODY",BODY,{"disambiguationData":[OSD([sQuery(id+"F0.wireOp",EDGE,"E0.bottom"),sQuery(id+"F0.wireOp",EDGE,"E0.top"),sQuery(id+"F0.wireOp",EDGE,"E0.left"),sQuery(id+"F0.wireOp",EDGE,"E0.right")])]}),"instanceName":"1"}),"instanceName":"1"}),"instanceName":"1"}),"instanceName":"1"}),"instanceName":"1"}),"instanceName":"1"}),"instanceName":"1"});
            deleteBodies(context, id + "F13", {"entities" : qUnion([Q0, Q1, Q2, Q3, Q4, Q5, Q6, Q7, Q8, Q9, Q10, Q11, Q12, Q13, Q14, Q15, Q16, Q17, Q18, Q19])});
        }
        {
            var Q0;
            Q0=makeQuery(id+"F1.opExtrude","SWEPT_BODY",BODY,{"disambiguationData":[OSD([sQuery(id+"F0.wireOp",EDGE,"E0.bottom"),sQuery(id+"F0.wireOp",EDGE,"E0.top"),sQuery(id+"F0.wireOp",EDGE,"E0.left"),sQuery(id+"F0.wireOp",EDGE,"E0.right")])]});
            var Q1;
            Q1=makeQuery(id+"F7.opPattern","COPY",BODY,{"derivedFrom":makeQuery(id+"F6.opPattern","COPY",BODY,{"derivedFrom":makeQuery(id+"F5.opPattern","COPY",BODY,{"derivedFrom":makeQuery(id+"F4.opPattern","COPY",BODY,{"derivedFrom":makeQuery(id+"F1.opExtrude","SWEPT_BODY",BODY,{"disambiguationData":[OSD([sQuery(id+"F0.wireOp",EDGE,"E0.bottom"),sQuery(id+"F0.wireOp",EDGE,"E0.top"),sQuery(id+"F0.wireOp",EDGE,"E0.left"),sQuery(id+"F0.wireOp",EDGE,"E0.right")])]}),"instanceName":"1"}),"instanceName":"1"}),"instanceName":"1"}),"instanceName":"1"});
            var Q2;
            Q2=makeQuery(id+"F6.opPattern","COPY",BODY,{"derivedFrom":makeQuery(id+"F5.opPattern","COPY",BODY,{"derivedFrom":makeQuery(id+"F4.opPattern","COPY",BODY,{"derivedFrom":makeQuery(id+"F1.opExtrude","SWEPT_BODY",BODY,{"disambiguationData":[OSD([sQuery(id+"F0.wireOp",EDGE,"E0.bottom"),sQuery(id+"F0.wireOp",EDGE,"E0.top"),sQuery(id+"F0.wireOp",EDGE,"E0.left"),sQuery(id+"F0.wireOp",EDGE,"E0.right")])]}),"instanceName":"1"}),"instanceName":"1"}),"instanceName":"1"});
            var Q3;
            Q3=makeQuery(id+"F5.opPattern","COPY",BODY,{"derivedFrom":makeQuery(id+"F4.opPattern","COPY",BODY,{"derivedFrom":makeQuery(id+"F1.opExtrude","SWEPT_BODY",BODY,{"disambiguationData":[OSD([sQuery(id+"F0.wireOp",EDGE,"E0.bottom"),sQuery(id+"F0.wireOp",EDGE,"E0.top"),sQuery(id+"F0.wireOp",EDGE,"E0.left"),sQuery(id+"F0.wireOp",EDGE,"E0.right")])]}),"instanceName":"1"}),"instanceName":"1"});
            var Q4;
            Q4=makeQuery(id+"F4.opPattern","COPY",BODY,{"derivedFrom":makeQuery(id+"F1.opExtrude","SWEPT_BODY",BODY,{"disambiguationData":[OSD([sQuery(id+"F0.wireOp",EDGE,"E0.bottom"),sQuery(id+"F0.wireOp",EDGE,"E0.top"),sQuery(id+"F0.wireOp",EDGE,"E0.left"),sQuery(id+"F0.wireOp",EDGE,"E0.right")])]}),"instanceName":"1"});
            transform(context, id + "F14", {"entities" : qUnion([Q0, Q1, Q2, Q3, Q4]), "transformType" : TransformType.TRANSLATION_3D, "dx" : 0 * mm, "dy" : 0 * mm, "dz" : 53.97 * mm, "makeCopy" : true});
        }
        {
            var Q0;
            Q0=makeQuery(id+"F14.opPattern","COPY",BODY,{"derivedFrom":makeQuery(id+"F1.opExtrude","SWEPT_BODY",BODY,{"disambiguationData":[OSD([sQuery(id+"F0.wireOp",EDGE,"E0.bottom"),sQuery(id+"F0.wireOp",EDGE,"E0.top"),sQuery(id+"F0.wireOp",EDGE,"E0.left"),sQuery(id+"F0.wireOp",EDGE,"E0.right")])]}),"instanceName":"1"});
            var Q1;
            Q1=makeQuery(id+"F14.opPattern","COPY",BODY,{"derivedFrom":makeQuery(id+"F7.opPattern","COPY",BODY,{"derivedFrom":makeQuery(id+"F6.opPattern","COPY",BODY,{"derivedFrom":makeQuery(id+"F5.opPattern","COPY",BODY,{"derivedFrom":makeQuery(id+"F4.opPattern","COPY",BODY,{"derivedFrom":makeQuery(id+"F1.opExtrude","SWEPT_BODY",BODY,{"disambiguationData":[OSD([sQuery(id+"F0.wireOp",EDGE,"E0.bottom"),sQuery(id+"F0.wireOp",EDGE,"E0.top"),sQuery(id+"F0.wireOp",EDGE,"E0.left"),sQuery(id+"F0.wireOp",EDGE,"E0.right")])]}),"instanceName":"1"}),"instanceName":"1"}),"instanceName":"1"}),"instanceName":"1"}),"instanceName":"1"});
            var Q2;
            Q2=makeQuery(id+"F14.opPattern","COPY",BODY,{"derivedFrom":makeQuery(id+"F6.opPattern","COPY",BODY,{"derivedFrom":makeQuery(id+"F5.opPattern","COPY",BODY,{"derivedFrom":makeQuery(id+"F4.opPattern","COPY",BODY,{"derivedFrom":makeQuery(id+"F1.opExtrude","SWEPT_BODY",BODY,{"disambiguationData":[OSD([sQuery(id+"F0.wireOp",EDGE,"E0.bottom"),sQuery(id+"F0.wireOp",EDGE,"E0.top"),sQuery(id+"F0.wireOp",EDGE,"E0.left"),sQuery(id+"F0.wireOp",EDGE,"E0.right")])]}),"instanceName":"1"}),"instanceName":"1"}),"instanceName":"1"}),"instanceName":"1"});
            var Q3;
            Q3=makeQuery(id+"F14.opPattern","COPY",BODY,{"derivedFrom":makeQuery(id+"F5.opPattern","COPY",BODY,{"derivedFrom":makeQuery(id+"F4.opPattern","COPY",BODY,{"derivedFrom":makeQuery(id+"F1.opExtrude","SWEPT_BODY",BODY,{"disambiguationData":[OSD([sQuery(id+"F0.wireOp",EDGE,"E0.bottom"),sQuery(id+"F0.wireOp",EDGE,"E0.top"),sQuery(id+"F0.wireOp",EDGE,"E0.left"),sQuery(id+"F0.wireOp",EDGE,"E0.right")])]}),"instanceName":"1"}),"instanceName":"1"}),"instanceName":"1"});
            var Q4;
            Q4=makeQuery(id+"F14.opPattern","COPY",BODY,{"derivedFrom":makeQuery(id+"F4.opPattern","COPY",BODY,{"derivedFrom":makeQuery(id+"F1.opExtrude","SWEPT_BODY",BODY,{"disambiguationData":[OSD([sQuery(id+"F0.wireOp",EDGE,"E0.bottom"),sQuery(id+"F0.wireOp",EDGE,"E0.top"),sQuery(id+"F0.wireOp",EDGE,"E0.left"),sQuery(id+"F0.wireOp",EDGE,"E0.right")])]}),"instanceName":"1"}),"instanceName":"1"});
            transform(context, id + "F15", {"entities" : qUnion([Q0, Q1, Q2, Q3, Q4]), "transformType" : TransformType.TRANSLATION_3D, "dx" : 0 * mm, "dy" : 0 * mm, "dz" : 53.97 * mm, "makeCopy" : true});
        }
        {
            var Q0;
            Q0=makeQuery(id+"F15.opPattern","COPY",BODY,{"derivedFrom":makeQuery(id+"F14.opPattern","COPY",BODY,{"derivedFrom":makeQuery(id+"F1.opExtrude","SWEPT_BODY",BODY,{"disambiguationData":[OSD([sQuery(id+"F0.wireOp",EDGE,"E0.bottom"),sQuery(id+"F0.wireOp",EDGE,"E0.top"),sQuery(id+"F0.wireOp",EDGE,"E0.left"),sQuery(id+"F0.wireOp",EDGE,"E0.right")])]}),"instanceName":"1"}),"instanceName":"1"});
            var Q1;
            Q1=makeQuery(id+"F15.opPattern","COPY",BODY,{"derivedFrom":makeQuery(id+"F14.opPattern","COPY",BODY,{"derivedFrom":makeQuery(id+"F4.opPattern","COPY",BODY,{"derivedFrom":makeQuery(id+"F1.opExtrude","SWEPT_BODY",BODY,{"disambiguationData":[OSD([sQuery(id+"F0.wireOp",EDGE,"E0.bottom"),sQuery(id+"F0.wireOp",EDGE,"E0.top"),sQuery(id+"F0.wireOp",EDGE,"E0.left"),sQuery(id+"F0.wireOp",EDGE,"E0.right")])]}),"instanceName":"1"}),"instanceName":"1"}),"instanceName":"1"});
            var Q2;
            Q2=makeQuery(id+"F15.opPattern","COPY",BODY,{"derivedFrom":makeQuery(id+"F14.opPattern","COPY",BODY,{"derivedFrom":makeQuery(id+"F5.opPattern","COPY",BODY,{"derivedFrom":makeQuery(id+"F4.opPattern","COPY",BODY,{"derivedFrom":makeQuery(id+"F1.opExtrude","SWEPT_BODY",BODY,{"disambiguationData":[OSD([sQuery(id+"F0.wireOp",EDGE,"E0.bottom"),sQuery(id+"F0.wireOp",EDGE,"E0.top"),sQuery(id+"F0.wireOp",EDGE,"E0.left"),sQuery(id+"F0.wireOp",EDGE,"E0.right")])]}),"instanceName":"1"}),"instanceName":"1"}),"instanceName":"1"}),"instanceName":"1"});
            var Q3;
            Q3=makeQuery(id+"F15.opPattern","COPY",BODY,{"derivedFrom":makeQuery(id+"F14.opPattern","COPY",BODY,{"derivedFrom":makeQuery(id+"F6.opPattern","COPY",BODY,{"derivedFrom":makeQuery(id+"F5.opPattern","COPY",BODY,{"derivedFrom":makeQuery(id+"F4.opPattern","COPY",BODY,{"derivedFrom":makeQuery(id+"F1.opExtrude","SWEPT_BODY",BODY,{"disambiguationData":[OSD([sQuery(id+"F0.wireOp",EDGE,"E0.bottom"),sQuery(id+"F0.wireOp",EDGE,"E0.top"),sQuery(id+"F0.wireOp",EDGE,"E0.left"),sQuery(id+"F0.wireOp",EDGE,"E0.right")])]}),"instanceName":"1"}),"instanceName":"1"}),"instanceName":"1"}),"instanceName":"1"}),"instanceName":"1"});
            var Q4;
            Q4=makeQuery(id+"F15.opPattern","COPY",BODY,{"derivedFrom":makeQuery(id+"F14.opPattern","COPY",BODY,{"derivedFrom":makeQuery(id+"F7.opPattern","COPY",BODY,{"derivedFrom":makeQuery(id+"F6.opPattern","COPY",BODY,{"derivedFrom":makeQuery(id+"F5.opPattern","COPY",BODY,{"derivedFrom":makeQuery(id+"F4.opPattern","COPY",BODY,{"derivedFrom":makeQuery(id+"F1.opExtrude","SWEPT_BODY",BODY,{"disambiguationData":[OSD([sQuery(id+"F0.wireOp",EDGE,"E0.bottom"),sQuery(id+"F0.wireOp",EDGE,"E0.top"),sQuery(id+"F0.wireOp",EDGE,"E0.left"),sQuery(id+"F0.wireOp",EDGE,"E0.right")])]}),"instanceName":"1"}),"instanceName":"1"}),"instanceName":"1"}),"instanceName":"1"}),"instanceName":"1"}),"instanceName":"1"});
            transform(context, id + "F16", {"entities" : qUnion([Q0, Q1, Q2, Q3, Q4]), "transformType" : TransformType.TRANSLATION_3D, "dx" : 0 * mm, "dy" : 0 * mm, "dz" : 53.97 * mm, "makeCopy" : true});
        }
        {
            var Q0;
            Q0=makeQuery(id+"F16.opPattern","COPY",BODY,{"derivedFrom":makeQuery(id+"F15.opPattern","COPY",BODY,{"derivedFrom":makeQuery(id+"F14.opPattern","COPY",BODY,{"derivedFrom":makeQuery(id+"F1.opExtrude","SWEPT_BODY",BODY,{"disambiguationData":[OSD([sQuery(id+"F0.wireOp",EDGE,"E0.bottom"),sQuery(id+"F0.wireOp",EDGE,"E0.top"),sQuery(id+"F0.wireOp",EDGE,"E0.left"),sQuery(id+"F0.wireOp",EDGE,"E0.right")])]}),"instanceName":"1"}),"instanceName":"1"}),"instanceName":"1"});
            var Q1;
            Q1=makeQuery(id+"F16.opPattern","COPY",BODY,{"derivedFrom":makeQuery(id+"F15.opPattern","COPY",BODY,{"derivedFrom":makeQuery(id+"F14.opPattern","COPY",BODY,{"derivedFrom":makeQuery(id+"F4.opPattern","COPY",BODY,{"derivedFrom":makeQuery(id+"F1.opExtrude","SWEPT_BODY",BODY,{"disambiguationData":[OSD([sQuery(id+"F0.wireOp",EDGE,"E0.bottom"),sQuery(id+"F0.wireOp",EDGE,"E0.top"),sQuery(id+"F0.wireOp",EDGE,"E0.left"),sQuery(id+"F0.wireOp",EDGE,"E0.right")])]}),"instanceName":"1"}),"instanceName":"1"}),"instanceName":"1"}),"instanceName":"1"});
            var Q2;
            Q2=makeQuery(id+"F16.opPattern","COPY",BODY,{"derivedFrom":makeQuery(id+"F15.opPattern","COPY",BODY,{"derivedFrom":makeQuery(id+"F14.opPattern","COPY",BODY,{"derivedFrom":makeQuery(id+"F5.opPattern","COPY",BODY,{"derivedFrom":makeQuery(id+"F4.opPattern","COPY",BODY,{"derivedFrom":makeQuery(id+"F1.opExtrude","SWEPT_BODY",BODY,{"disambiguationData":[OSD([sQuery(id+"F0.wireOp",EDGE,"E0.bottom"),sQuery(id+"F0.wireOp",EDGE,"E0.top"),sQuery(id+"F0.wireOp",EDGE,"E0.left"),sQuery(id+"F0.wireOp",EDGE,"E0.right")])]}),"instanceName":"1"}),"instanceName":"1"}),"instanceName":"1"}),"instanceName":"1"}),"instanceName":"1"});
            var Q3;
            Q3=makeQuery(id+"F16.opPattern","COPY",BODY,{"derivedFrom":makeQuery(id+"F15.opPattern","COPY",BODY,{"derivedFrom":makeQuery(id+"F14.opPattern","COPY",BODY,{"derivedFrom":makeQuery(id+"F7.opPattern","COPY",BODY,{"derivedFrom":makeQuery(id+"F6.opPattern","COPY",BODY,{"derivedFrom":makeQuery(id+"F5.opPattern","COPY",BODY,{"derivedFrom":makeQuery(id+"F4.opPattern","COPY",BODY,{"derivedFrom":makeQuery(id+"F1.opExtrude","SWEPT_BODY",BODY,{"disambiguationData":[OSD([sQuery(id+"F0.wireOp",EDGE,"E0.bottom"),sQuery(id+"F0.wireOp",EDGE,"E0.top"),sQuery(id+"F0.wireOp",EDGE,"E0.left"),sQuery(id+"F0.wireOp",EDGE,"E0.right")])]}),"instanceName":"1"}),"instanceName":"1"}),"instanceName":"1"}),"instanceName":"1"}),"instanceName":"1"}),"instanceName":"1"}),"instanceName":"1"});
            var Q4;
            Q4=makeQuery(id+"F16.opPattern","COPY",BODY,{"derivedFrom":makeQuery(id+"F15.opPattern","COPY",BODY,{"derivedFrom":makeQuery(id+"F14.opPattern","COPY",BODY,{"derivedFrom":makeQuery(id+"F6.opPattern","COPY",BODY,{"derivedFrom":makeQuery(id+"F5.opPattern","COPY",BODY,{"derivedFrom":makeQuery(id+"F4.opPattern","COPY",BODY,{"derivedFrom":makeQuery(id+"F1.opExtrude","SWEPT_BODY",BODY,{"disambiguationData":[OSD([sQuery(id+"F0.wireOp",EDGE,"E0.bottom"),sQuery(id+"F0.wireOp",EDGE,"E0.top"),sQuery(id+"F0.wireOp",EDGE,"E0.left"),sQuery(id+"F0.wireOp",EDGE,"E0.right")])]}),"instanceName":"1"}),"instanceName":"1"}),"instanceName":"1"}),"instanceName":"1"}),"instanceName":"1"}),"instanceName":"1"});
            transform(context, id + "F17", {"entities" : qUnion([Q0, Q1, Q2, Q3, Q4]), "transformType" : TransformType.TRANSLATION_3D, "dx" : 0 * mm, "dy" : 0 * mm, "dz" : 53.97 * mm, "makeCopy" : true});
        }
        {
            var Q0;
            Q0=makeQuery(id+"F1.opExtrude","SWEPT_BODY",BODY,{"disambiguationData":[OSD([sQuery(id+"F0.wireOp",EDGE,"E0.bottom"),sQuery(id+"F0.wireOp",EDGE,"E0.top"),sQuery(id+"F0.wireOp",EDGE,"E0.left"),sQuery(id+"F0.wireOp",EDGE,"E0.right")])]});
            var Q1;
            Q1=makeQuery(id+"F5.opPattern","COPY",BODY,{"derivedFrom":makeQuery(id+"F4.opPattern","COPY",BODY,{"derivedFrom":makeQuery(id+"F1.opExtrude","SWEPT_BODY",BODY,{"disambiguationData":[OSD([sQuery(id+"F0.wireOp",EDGE,"E0.bottom"),sQuery(id+"F0.wireOp",EDGE,"E0.top"),sQuery(id+"F0.wireOp",EDGE,"E0.left"),sQuery(id+"F0.wireOp",EDGE,"E0.right")])]}),"instanceName":"1"}),"instanceName":"1"});
            var Q2;
            Q2=makeQuery(id+"F7.opPattern","COPY",BODY,{"derivedFrom":makeQuery(id+"F6.opPattern","COPY",BODY,{"derivedFrom":makeQuery(id+"F5.opPattern","COPY",BODY,{"derivedFrom":makeQuery(id+"F4.opPattern","COPY",BODY,{"derivedFrom":makeQuery(id+"F1.opExtrude","SWEPT_BODY",BODY,{"disambiguationData":[OSD([sQuery(id+"F0.wireOp",EDGE,"E0.bottom"),sQuery(id+"F0.wireOp",EDGE,"E0.top"),sQuery(id+"F0.wireOp",EDGE,"E0.left"),sQuery(id+"F0.wireOp",EDGE,"E0.right")])]}),"instanceName":"1"}),"instanceName":"1"}),"instanceName":"1"}),"instanceName":"1"});
            var Q3;
            Q3=makeQuery(id+"F14.opPattern","COPY",BODY,{"derivedFrom":makeQuery(id+"F6.opPattern","COPY",BODY,{"derivedFrom":makeQuery(id+"F5.opPattern","COPY",BODY,{"derivedFrom":makeQuery(id+"F4.opPattern","COPY",BODY,{"derivedFrom":makeQuery(id+"F1.opExtrude","SWEPT_BODY",BODY,{"disambiguationData":[OSD([sQuery(id+"F0.wireOp",EDGE,"E0.bottom"),sQuery(id+"F0.wireOp",EDGE,"E0.top"),sQuery(id+"F0.wireOp",EDGE,"E0.left"),sQuery(id+"F0.wireOp",EDGE,"E0.right")])]}),"instanceName":"1"}),"instanceName":"1"}),"instanceName":"1"}),"instanceName":"1"});
            var Q4;
            Q4=makeQuery(id+"F14.opPattern","COPY",BODY,{"derivedFrom":makeQuery(id+"F4.opPattern","COPY",BODY,{"derivedFrom":makeQuery(id+"F1.opExtrude","SWEPT_BODY",BODY,{"disambiguationData":[OSD([sQuery(id+"F0.wireOp",EDGE,"E0.bottom"),sQuery(id+"F0.wireOp",EDGE,"E0.top"),sQuery(id+"F0.wireOp",EDGE,"E0.left"),sQuery(id+"F0.wireOp",EDGE,"E0.right")])]}),"instanceName":"1"}),"instanceName":"1"});
            var Q5;
            Q5=makeQuery(id+"F15.opPattern","COPY",BODY,{"derivedFrom":makeQuery(id+"F14.opPattern","COPY",BODY,{"derivedFrom":makeQuery(id+"F1.opExtrude","SWEPT_BODY",BODY,{"disambiguationData":[OSD([sQuery(id+"F0.wireOp",EDGE,"E0.bottom"),sQuery(id+"F0.wireOp",EDGE,"E0.top"),sQuery(id+"F0.wireOp",EDGE,"E0.left"),sQuery(id+"F0.wireOp",EDGE,"E0.right")])]}),"instanceName":"1"}),"instanceName":"1"});
            var Q6;
            Q6=makeQuery(id+"F15.opPattern","COPY",BODY,{"derivedFrom":makeQuery(id+"F14.opPattern","COPY",BODY,{"derivedFrom":makeQuery(id+"F5.opPattern","COPY",BODY,{"derivedFrom":makeQuery(id+"F4.opPattern","COPY",BODY,{"derivedFrom":makeQuery(id+"F1.opExtrude","SWEPT_BODY",BODY,{"disambiguationData":[OSD([sQuery(id+"F0.wireOp",EDGE,"E0.bottom"),sQuery(id+"F0.wireOp",EDGE,"E0.top"),sQuery(id+"F0.wireOp",EDGE,"E0.left"),sQuery(id+"F0.wireOp",EDGE,"E0.right")])]}),"instanceName":"1"}),"instanceName":"1"}),"instanceName":"1"}),"instanceName":"1"});
            var Q7;
            Q7=makeQuery(id+"F15.opPattern","COPY",BODY,{"derivedFrom":makeQuery(id+"F14.opPattern","COPY",BODY,{"derivedFrom":makeQuery(id+"F7.opPattern","COPY",BODY,{"derivedFrom":makeQuery(id+"F6.opPattern","COPY",BODY,{"derivedFrom":makeQuery(id+"F5.opPattern","COPY",BODY,{"derivedFrom":makeQuery(id+"F4.opPattern","COPY",BODY,{"derivedFrom":makeQuery(id+"F1.opExtrude","SWEPT_BODY",BODY,{"disambiguationData":[OSD([sQuery(id+"F0.wireOp",EDGE,"E0.bottom"),sQuery(id+"F0.wireOp",EDGE,"E0.top"),sQuery(id+"F0.wireOp",EDGE,"E0.left"),sQuery(id+"F0.wireOp",EDGE,"E0.right")])]}),"instanceName":"1"}),"instanceName":"1"}),"instanceName":"1"}),"instanceName":"1"}),"instanceName":"1"}),"instanceName":"1"});
            var Q8;
            Q8=makeQuery(id+"F16.opPattern","COPY",BODY,{"derivedFrom":makeQuery(id+"F15.opPattern","COPY",BODY,{"derivedFrom":makeQuery(id+"F14.opPattern","COPY",BODY,{"derivedFrom":makeQuery(id+"F6.opPattern","COPY",BODY,{"derivedFrom":makeQuery(id+"F5.opPattern","COPY",BODY,{"derivedFrom":makeQuery(id+"F4.opPattern","COPY",BODY,{"derivedFrom":makeQuery(id+"F1.opExtrude","SWEPT_BODY",BODY,{"disambiguationData":[OSD([sQuery(id+"F0.wireOp",EDGE,"E0.bottom"),sQuery(id+"F0.wireOp",EDGE,"E0.top"),sQuery(id+"F0.wireOp",EDGE,"E0.left"),sQuery(id+"F0.wireOp",EDGE,"E0.right")])]}),"instanceName":"1"}),"instanceName":"1"}),"instanceName":"1"}),"instanceName":"1"}),"instanceName":"1"}),"instanceName":"1"});
            var Q9;
            Q9=makeQuery(id+"F16.opPattern","COPY",BODY,{"derivedFrom":makeQuery(id+"F15.opPattern","COPY",BODY,{"derivedFrom":makeQuery(id+"F14.opPattern","COPY",BODY,{"derivedFrom":makeQuery(id+"F4.opPattern","COPY",BODY,{"derivedFrom":makeQuery(id+"F1.opExtrude","SWEPT_BODY",BODY,{"disambiguationData":[OSD([sQuery(id+"F0.wireOp",EDGE,"E0.bottom"),sQuery(id+"F0.wireOp",EDGE,"E0.top"),sQuery(id+"F0.wireOp",EDGE,"E0.left"),sQuery(id+"F0.wireOp",EDGE,"E0.right")])]}),"instanceName":"1"}),"instanceName":"1"}),"instanceName":"1"}),"instanceName":"1"});
            var Q10;
            Q10=makeQuery(id+"F17.opPattern","COPY",BODY,{"derivedFrom":makeQuery(id+"F16.opPattern","COPY",BODY,{"derivedFrom":makeQuery(id+"F15.opPattern","COPY",BODY,{"derivedFrom":makeQuery(id+"F14.opPattern","COPY",BODY,{"derivedFrom":makeQuery(id+"F1.opExtrude","SWEPT_BODY",BODY,{"disambiguationData":[OSD([sQuery(id+"F0.wireOp",EDGE,"E0.bottom"),sQuery(id+"F0.wireOp",EDGE,"E0.top"),sQuery(id+"F0.wireOp",EDGE,"E0.left"),sQuery(id+"F0.wireOp",EDGE,"E0.right")])]}),"instanceName":"1"}),"instanceName":"1"}),"instanceName":"1"}),"instanceName":"1"});
            var Q11;
            Q11=makeQuery(id+"F17.opPattern","COPY",BODY,{"derivedFrom":makeQuery(id+"F16.opPattern","COPY",BODY,{"derivedFrom":makeQuery(id+"F15.opPattern","COPY",BODY,{"derivedFrom":makeQuery(id+"F14.opPattern","COPY",BODY,{"derivedFrom":makeQuery(id+"F5.opPattern","COPY",BODY,{"derivedFrom":makeQuery(id+"F4.opPattern","COPY",BODY,{"derivedFrom":makeQuery(id+"F1.opExtrude","SWEPT_BODY",BODY,{"disambiguationData":[OSD([sQuery(id+"F0.wireOp",EDGE,"E0.bottom"),sQuery(id+"F0.wireOp",EDGE,"E0.top"),sQuery(id+"F0.wireOp",EDGE,"E0.left"),sQuery(id+"F0.wireOp",EDGE,"E0.right")])]}),"instanceName":"1"}),"instanceName":"1"}),"instanceName":"1"}),"instanceName":"1"}),"instanceName":"1"}),"instanceName":"1"});
            var Q12;
            Q12=makeQuery(id+"F17.opPattern","COPY",BODY,{"derivedFrom":makeQuery(id+"F16.opPattern","COPY",BODY,{"derivedFrom":makeQuery(id+"F15.opPattern","COPY",BODY,{"derivedFrom":makeQuery(id+"F14.opPattern","COPY",BODY,{"derivedFrom":makeQuery(id+"F7.opPattern","COPY",BODY,{"derivedFrom":makeQuery(id+"F6.opPattern","COPY",BODY,{"derivedFrom":makeQuery(id+"F5.opPattern","COPY",BODY,{"derivedFrom":makeQuery(id+"F4.opPattern","COPY",BODY,{"derivedFrom":makeQuery(id+"F1.opExtrude","SWEPT_BODY",BODY,{"disambiguationData":[OSD([sQuery(id+"F0.wireOp",EDGE,"E0.bottom"),sQuery(id+"F0.wireOp",EDGE,"E0.top"),sQuery(id+"F0.wireOp",EDGE,"E0.left"),sQuery(id+"F0.wireOp",EDGE,"E0.right")])]}),"instanceName":"1"}),"instanceName":"1"}),"instanceName":"1"}),"instanceName":"1"}),"instanceName":"1"}),"instanceName":"1"}),"instanceName":"1"}),"instanceName":"1"});
            deleteBodies(context, id + "F18", {"entities" : qUnion([Q0, Q1, Q2, Q3, Q4, Q5, Q6, Q7, Q8, Q9, Q10, Q11, Q12])});
        }
        {
            var Q0;
            Q0=makeQuery(id+"F4.opPattern","COPY",BODY,{"derivedFrom":makeQuery(id+"F1.opExtrude","SWEPT_BODY",BODY,{"disambiguationData":[OSD([sQuery(id+"F0.wireOp",EDGE,"E0.bottom"),sQuery(id+"F0.wireOp",EDGE,"E0.top"),sQuery(id+"F0.wireOp",EDGE,"E0.left"),sQuery(id+"F0.wireOp",EDGE,"E0.right")])]}),"instanceName":"1"});
            var Q1;
            Q1=makeQuery(id+"F6.opPattern","COPY",BODY,{"derivedFrom":makeQuery(id+"F5.opPattern","COPY",BODY,{"derivedFrom":makeQuery(id+"F4.opPattern","COPY",BODY,{"derivedFrom":makeQuery(id+"F1.opExtrude","SWEPT_BODY",BODY,{"disambiguationData":[OSD([sQuery(id+"F0.wireOp",EDGE,"E0.bottom"),sQuery(id+"F0.wireOp",EDGE,"E0.top"),sQuery(id+"F0.wireOp",EDGE,"E0.left"),sQuery(id+"F0.wireOp",EDGE,"E0.right")])]}),"instanceName":"1"}),"instanceName":"1"}),"instanceName":"1"});
            var Q2;
            Q2=makeQuery(id+"F14.opPattern","COPY",BODY,{"derivedFrom":makeQuery(id+"F1.opExtrude","SWEPT_BODY",BODY,{"disambiguationData":[OSD([sQuery(id+"F0.wireOp",EDGE,"E0.bottom"),sQuery(id+"F0.wireOp",EDGE,"E0.top"),sQuery(id+"F0.wireOp",EDGE,"E0.left"),sQuery(id+"F0.wireOp",EDGE,"E0.right")])]}),"instanceName":"1"});
            var Q3;
            Q3=makeQuery(id+"F14.opPattern","COPY",BODY,{"derivedFrom":makeQuery(id+"F5.opPattern","COPY",BODY,{"derivedFrom":makeQuery(id+"F4.opPattern","COPY",BODY,{"derivedFrom":makeQuery(id+"F1.opExtrude","SWEPT_BODY",BODY,{"disambiguationData":[OSD([sQuery(id+"F0.wireOp",EDGE,"E0.bottom"),sQuery(id+"F0.wireOp",EDGE,"E0.top"),sQuery(id+"F0.wireOp",EDGE,"E0.left"),sQuery(id+"F0.wireOp",EDGE,"E0.right")])]}),"instanceName":"1"}),"instanceName":"1"}),"instanceName":"1"});
            var Q4;
            Q4=makeQuery(id+"F14.opPattern","COPY",BODY,{"derivedFrom":makeQuery(id+"F7.opPattern","COPY",BODY,{"derivedFrom":makeQuery(id+"F6.opPattern","COPY",BODY,{"derivedFrom":makeQuery(id+"F5.opPattern","COPY",BODY,{"derivedFrom":makeQuery(id+"F4.opPattern","COPY",BODY,{"derivedFrom":makeQuery(id+"F1.opExtrude","SWEPT_BODY",BODY,{"disambiguationData":[OSD([sQuery(id+"F0.wireOp",EDGE,"E0.bottom"),sQuery(id+"F0.wireOp",EDGE,"E0.top"),sQuery(id+"F0.wireOp",EDGE,"E0.left"),sQuery(id+"F0.wireOp",EDGE,"E0.right")])]}),"instanceName":"1"}),"instanceName":"1"}),"instanceName":"1"}),"instanceName":"1"}),"instanceName":"1"});
            var Q5;
            Q5=makeQuery(id+"F15.opPattern","COPY",BODY,{"derivedFrom":makeQuery(id+"F14.opPattern","COPY",BODY,{"derivedFrom":makeQuery(id+"F4.opPattern","COPY",BODY,{"derivedFrom":makeQuery(id+"F1.opExtrude","SWEPT_BODY",BODY,{"disambiguationData":[OSD([sQuery(id+"F0.wireOp",EDGE,"E0.bottom"),sQuery(id+"F0.wireOp",EDGE,"E0.top"),sQuery(id+"F0.wireOp",EDGE,"E0.left"),sQuery(id+"F0.wireOp",EDGE,"E0.right")])]}),"instanceName":"1"}),"instanceName":"1"}),"instanceName":"1"});
            var Q6;
            Q6=makeQuery(id+"F15.opPattern","COPY",BODY,{"derivedFrom":makeQuery(id+"F14.opPattern","COPY",BODY,{"derivedFrom":makeQuery(id+"F6.opPattern","COPY",BODY,{"derivedFrom":makeQuery(id+"F5.opPattern","COPY",BODY,{"derivedFrom":makeQuery(id+"F4.opPattern","COPY",BODY,{"derivedFrom":makeQuery(id+"F1.opExtrude","SWEPT_BODY",BODY,{"disambiguationData":[OSD([sQuery(id+"F0.wireOp",EDGE,"E0.bottom"),sQuery(id+"F0.wireOp",EDGE,"E0.top"),sQuery(id+"F0.wireOp",EDGE,"E0.left"),sQuery(id+"F0.wireOp",EDGE,"E0.right")])]}),"instanceName":"1"}),"instanceName":"1"}),"instanceName":"1"}),"instanceName":"1"}),"instanceName":"1"});
            var Q7;
            Q7=makeQuery(id+"F16.opPattern","COPY",BODY,{"derivedFrom":makeQuery(id+"F15.opPattern","COPY",BODY,{"derivedFrom":makeQuery(id+"F14.opPattern","COPY",BODY,{"derivedFrom":makeQuery(id+"F1.opExtrude","SWEPT_BODY",BODY,{"disambiguationData":[OSD([sQuery(id+"F0.wireOp",EDGE,"E0.bottom"),sQuery(id+"F0.wireOp",EDGE,"E0.top"),sQuery(id+"F0.wireOp",EDGE,"E0.left"),sQuery(id+"F0.wireOp",EDGE,"E0.right")])]}),"instanceName":"1"}),"instanceName":"1"}),"instanceName":"1"});
            var Q8;
            Q8=makeQuery(id+"F16.opPattern","COPY",BODY,{"derivedFrom":makeQuery(id+"F15.opPattern","COPY",BODY,{"derivedFrom":makeQuery(id+"F14.opPattern","COPY",BODY,{"derivedFrom":makeQuery(id+"F5.opPattern","COPY",BODY,{"derivedFrom":makeQuery(id+"F4.opPattern","COPY",BODY,{"derivedFrom":makeQuery(id+"F1.opExtrude","SWEPT_BODY",BODY,{"disambiguationData":[OSD([sQuery(id+"F0.wireOp",EDGE,"E0.bottom"),sQuery(id+"F0.wireOp",EDGE,"E0.top"),sQuery(id+"F0.wireOp",EDGE,"E0.left"),sQuery(id+"F0.wireOp",EDGE,"E0.right")])]}),"instanceName":"1"}),"instanceName":"1"}),"instanceName":"1"}),"instanceName":"1"}),"instanceName":"1"});
            var Q9;
            Q9=makeQuery(id+"F16.opPattern","COPY",BODY,{"derivedFrom":makeQuery(id+"F15.opPattern","COPY",BODY,{"derivedFrom":makeQuery(id+"F14.opPattern","COPY",BODY,{"derivedFrom":makeQuery(id+"F7.opPattern","COPY",BODY,{"derivedFrom":makeQuery(id+"F6.opPattern","COPY",BODY,{"derivedFrom":makeQuery(id+"F5.opPattern","COPY",BODY,{"derivedFrom":makeQuery(id+"F4.opPattern","COPY",BODY,{"derivedFrom":makeQuery(id+"F1.opExtrude","SWEPT_BODY",BODY,{"disambiguationData":[OSD([sQuery(id+"F0.wireOp",EDGE,"E0.bottom"),sQuery(id+"F0.wireOp",EDGE,"E0.top"),sQuery(id+"F0.wireOp",EDGE,"E0.left"),sQuery(id+"F0.wireOp",EDGE,"E0.right")])]}),"instanceName":"1"}),"instanceName":"1"}),"instanceName":"1"}),"instanceName":"1"}),"instanceName":"1"}),"instanceName":"1"}),"instanceName":"1"});
            var Q10;
            Q10=makeQuery(id+"F17.opPattern","COPY",BODY,{"derivedFrom":makeQuery(id+"F16.opPattern","COPY",BODY,{"derivedFrom":makeQuery(id+"F15.opPattern","COPY",BODY,{"derivedFrom":makeQuery(id+"F14.opPattern","COPY",BODY,{"derivedFrom":makeQuery(id+"F4.opPattern","COPY",BODY,{"derivedFrom":makeQuery(id+"F1.opExtrude","SWEPT_BODY",BODY,{"disambiguationData":[OSD([sQuery(id+"F0.wireOp",EDGE,"E0.bottom"),sQuery(id+"F0.wireOp",EDGE,"E0.top"),sQuery(id+"F0.wireOp",EDGE,"E0.left"),sQuery(id+"F0.wireOp",EDGE,"E0.right")])]}),"instanceName":"1"}),"instanceName":"1"}),"instanceName":"1"}),"instanceName":"1"}),"instanceName":"1"});
            var Q11;
            Q11=makeQuery(id+"F17.opPattern","COPY",BODY,{"derivedFrom":makeQuery(id+"F16.opPattern","COPY",BODY,{"derivedFrom":makeQuery(id+"F15.opPattern","COPY",BODY,{"derivedFrom":makeQuery(id+"F14.opPattern","COPY",BODY,{"derivedFrom":makeQuery(id+"F6.opPattern","COPY",BODY,{"derivedFrom":makeQuery(id+"F5.opPattern","COPY",BODY,{"derivedFrom":makeQuery(id+"F4.opPattern","COPY",BODY,{"derivedFrom":makeQuery(id+"F1.opExtrude","SWEPT_BODY",BODY,{"disambiguationData":[OSD([sQuery(id+"F0.wireOp",EDGE,"E0.bottom"),sQuery(id+"F0.wireOp",EDGE,"E0.top"),sQuery(id+"F0.wireOp",EDGE,"E0.left"),sQuery(id+"F0.wireOp",EDGE,"E0.right")])]}),"instanceName":"1"}),"instanceName":"1"}),"instanceName":"1"}),"instanceName":"1"}),"instanceName":"1"}),"instanceName":"1"}),"instanceName":"1"});
            transform(context, id + "F19", {"entities" : qUnion([Q0, Q1, Q2, Q3, Q4, Q5, Q6, Q7, Q8, Q9, Q10, Q11]), "transformType" : TransformType.TRANSLATION_3D, "dx" : 0 * mm, "dy" : 0.83 * mm, "dz" : 0 * mm, "makeCopy" : false});
        }
    });
